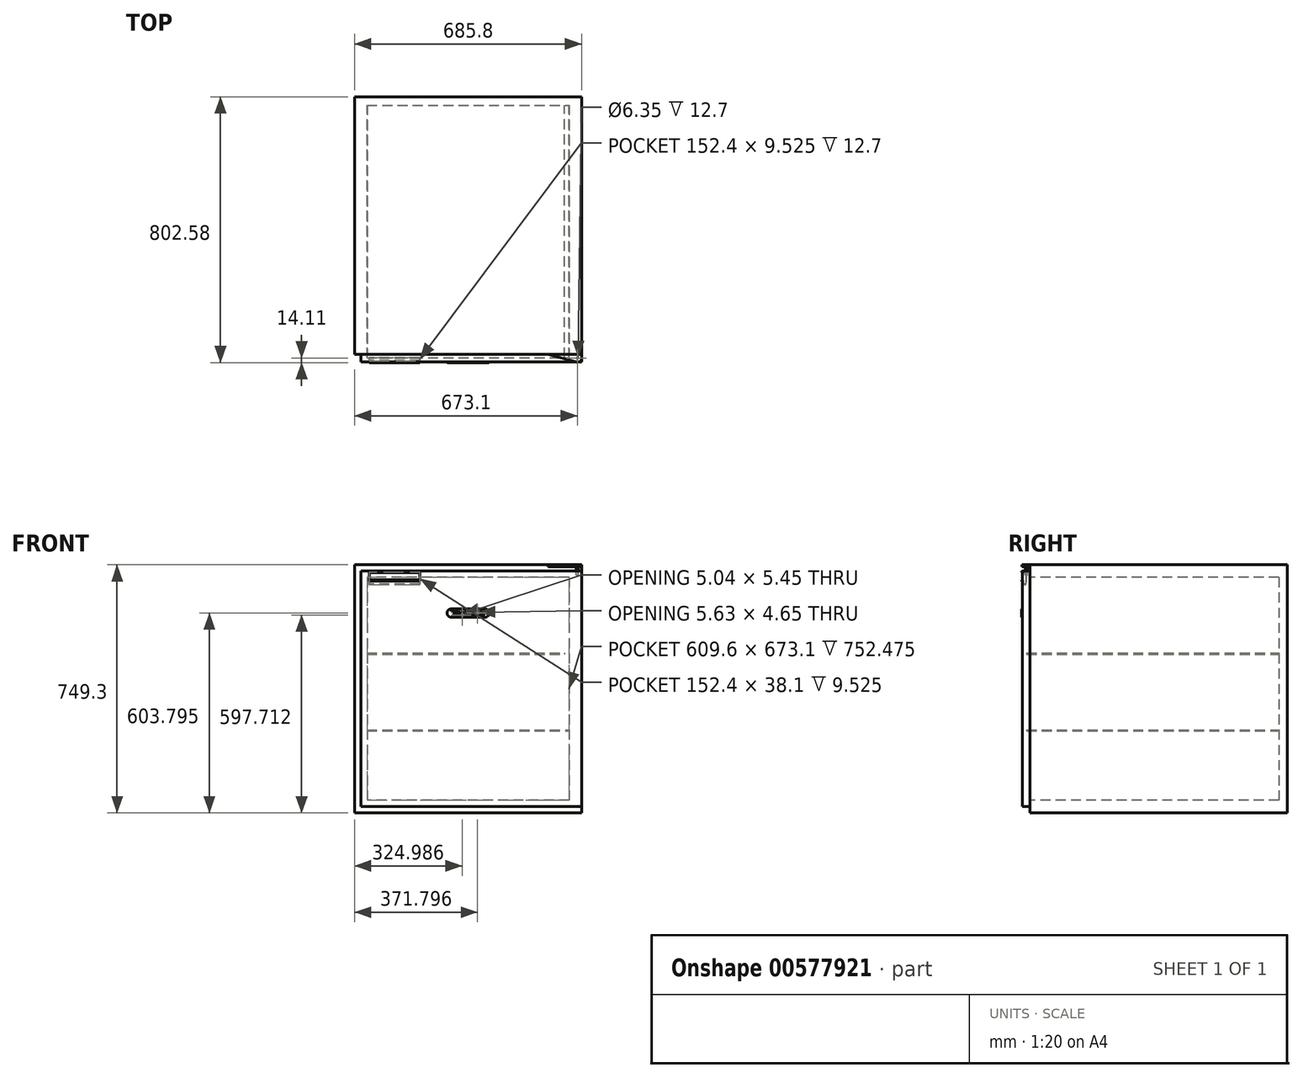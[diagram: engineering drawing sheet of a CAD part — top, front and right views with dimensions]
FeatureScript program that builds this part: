
annotation { "Feature Type Name" : "Feature", "Feature Type Description" : "" }
export const myFeature = defineFeature(function(context is Context, id is Id, definition is map)
    precondition{}
    {
        {
            var Q0;
            Q0=qCreatedBy(makeId("Front.planeOp"),FACE);
            var sketch = newSketch(context, id + "F0", { "sketchPlane" : qUnion([Q0])});
            skLineSegment(sketch, "E0.bottom", {"start": v(342.9, 374.65) * mm, "end": v(-342.9, 374.65) * mm});
            skLineSegment(sketch, "E0.top", {"start": v(342.9, -374.65) * mm, "end": v(-342.9, -374.65) * mm});
            skLineSegment(sketch, "E0.left", {"start": v(342.9, 374.65) * mm, "end": v(342.9, -374.65) * mm});
            skLineSegment(sketch, "E0.right", {"start": v(-342.9, 374.65) * mm, "end": v(-342.9, -374.65) * mm});
            skPoint(sketch, "E0.middle", {"position": v(0, 0) * mm});
            skLineSegment(sketch, "E1.0", {"start": v(304.8, 336.55) * mm, "end": v(-304.8, 336.55) * mm});
            skLineSegment(sketch, "E1.1", {"start": v(304.8, 336.55) * mm, "end": v(304.8, -336.55) * mm});
            skLineSegment(sketch, "E1.2", {"start": v(304.8, -336.55) * mm, "end": v(-304.8, -336.55) * mm});
            skLineSegment(sketch, "E1.3", {"start": v(-304.8, 336.55) * mm, "end": v(-304.8, -336.55) * mm});
            skSolve(sketch);
        }
        {
            var Q0;
            Q0=makeQuery(id+"F0.imprint","IMPRINT",FACE,{"disambiguationData":[TD([[makeQuery(id+"F0.imprint","IMPRINT",EDGE,{"derivedFrom":sQuery(id+"F0.wireOp",EDGE,"E0.bottom")}),1.0]])]});
            extrude(context, id + "F1", {"entities" : qUnion([Q0]), "oppositeDirection" : true, "depth" : 777.88 * mm, "offsetDistance" : 25.4 * mm});
        }
        {
            var Q0;
            Q0=makeQuery(id+"F1.opExtrude","CAP_FACE",FACE,{"disambiguationData":[OSD([sQuery(id+"F0.wireOp",EDGE,"E0.bottom"),sQuery(id+"F0.wireOp",EDGE,"E0.top"),sQuery(id+"F0.wireOp",EDGE,"E0.left"),sQuery(id+"F0.wireOp",EDGE,"E0.right"),sQuery(id+"F0.wireOp",EDGE,"E1.0"),sQuery(id+"F0.wireOp",EDGE,"E1.1"),sQuery(id+"F0.wireOp",EDGE,"E1.2"),sQuery(id+"F0.wireOp",EDGE,"E1.3")])],"isStart":false});
            var sketch = newSketch(context, id + "F2", { "sketchPlane" : qUnion([Q0])});
            skLineSegment(sketch, "E2.0", {"start": v(-342.9, 374.65) * mm, "end": v(342.9, 374.65) * mm});
            skLineSegment(sketch, "E3.0", {"start": v(342.9, 374.65) * mm, "end": v(342.9, -374.65) * mm});
            skLineSegment(sketch, "E3.1", {"start": v(-342.9, 374.65) * mm, "end": v(-342.9, -374.65) * mm});
            skLineSegment(sketch, "E3.2", {"start": v(-342.9, -374.65) * mm, "end": v(342.9, -374.65) * mm});
            skSolve(sketch);
        }
        {
            var Q0;
            Q0 = qSketchRegion(id + "F2", true);
            extrude(context, id + "F3", {"entities" : qUnion([Q0]), "operationType" : NewBodyOperationType.ADD, "oppositeDirection" : true, "depth" : 25.4 * mm, "offsetDistance" : 25.4 * mm});
        }
        {
            var Q0;
            Q0=makeQuery(id+"F3.opExtrude","CAP_FACE",FACE,{"disambiguationData":[OSD([sQuery(id+"F2.wireOp",EDGE,"E2.0"),sQuery(id+"F2.wireOp",EDGE,"E3.0"),sQuery(id+"F2.wireOp",EDGE,"E3.1"),sQuery(id+"F2.wireOp",EDGE,"E3.2")])],"isStart":false});
            var sketch = newSketch(context, id + "F4", { "sketchPlane" : qUnion([Q0])});
            skLineSegment(sketch, "E4.bottom", {"start": v(-304.8, 107.95) * mm, "end": v(290.97, 107.95) * mm});
            skLineSegment(sketch, "E4.top", {"start": v(-304.8, 104.78) * mm, "end": v(290.97, 104.78) * mm});
            skLineSegment(sketch, "E4.left", {"start": v(-304.8, 107.95) * mm, "end": v(-304.8, 104.78) * mm});
            skLineSegment(sketch, "E4.right", {"start": v(290.97, 107.95) * mm, "end": v(290.97, 104.78) * mm});
            skLineSegment(sketch, "E5.bottom", {"start": v(-304.8, -123.82) * mm, "end": v(304.8, -123.82) * mm});
            skLineSegment(sketch, "E5.top", {"start": v(-304.8, -127) * mm, "end": v(304.8, -127) * mm});
            skLineSegment(sketch, "E5.left", {"start": v(-304.8, -123.82) * mm, "end": v(-304.8, -127) * mm});
            skLineSegment(sketch, "E5.right", {"start": v(304.8, -123.82) * mm, "end": v(304.8, -127) * mm});
            skSolve(sketch);
        }
        {
            var Q0;
            Q0 = qSketchRegion(id + "F4", true);
            extrude(context, id + "F5", {"entities" : qUnion([Q0]), "depth" : 762 * mm, "offsetDistance" : 25.4 * mm});
        }
        {
            var Q0;
            Q0=makeQuery(id+"F1.opExtrude","CAP_FACE",FACE,{"disambiguationData":[OSD([sQuery(id+"F0.wireOp",EDGE,"E0.bottom"),sQuery(id+"F0.wireOp",EDGE,"E0.top"),sQuery(id+"F0.wireOp",EDGE,"E0.left"),sQuery(id+"F0.wireOp",EDGE,"E0.right"),sQuery(id+"F0.wireOp",EDGE,"E1.0"),sQuery(id+"F0.wireOp",EDGE,"E1.1"),sQuery(id+"F0.wireOp",EDGE,"E1.2"),sQuery(id+"F0.wireOp",EDGE,"E1.3")])],"isStart":true});
            var sketch = newSketch(context, id + "F6", { "sketchPlane" : qUnion([Q0])});
            skLineSegment(sketch, "E6.0", {"start": v(342.9, 355.6) * mm, "end": v(-323.85, 355.6) * mm});
            skLineSegment(sketch, "E6.2", {"start": v(342.9, -355.6) * mm, "end": v(-323.85, -355.6) * mm});
            skLineSegment(sketch, "E6.3", {"start": v(-323.85, 355.6) * mm, "end": v(-323.85, -355.6) * mm});
            skLineSegment(sketch, "E7", {"start": v(342.9, 355.6) * mm, "end": v(342.9, -355.6) * mm});
            skSolve(sketch);
        }
        {
            var Q0;
            Q0 = qSketchRegion(id + "F6", true);
            extrude(context, id + "F7", {"entities" : qUnion([Q0]), "depth" : 22.86 * mm, "offsetDistance" : 25.4 * mm});
        }
        {
            var Q0;
            Q0=makeQuery(id+"F1.opExtrude","SWEPT_FACE",FACE,{"disambiguationData":[OSD([sQuery(id+"F0.wireOp",EDGE,"E0.bottom")])]});
            var sketch = newSketch(context, id + "F8", { "sketchPlane" : qUnion([Q0])});
            skLineSegment(sketch, "E8", {"start": v(241.3, 0) * mm, "end": v(326.92, -22.86) * mm});
            skLineSegment(sketch, "E9", {"start": v(342.9, -10.59) * mm, "end": v(342.9, 0) * mm});
            skPoint(sketch, "E10.0", {"position": v(-323.85, -22.86) * mm});
            skLineSegment(sketch, "E11", {"start": v(241.3, 0) * mm, "end": v(342.9, 0) * mm});
            skPoint(sketch, "E12.visualSharp", {"position": v(342.9, -27.13) * mm});
            skArc(sketch, "E12.filletArc", {"start": v(326.92, -22.86) * mm, "mid": v(337.94, -20.66) * mm, "end": v(342.9, -10.59) * mm});
            skSolve(sketch);
        }
        {
            var Q0;
            Q0 = qSketchRegion(id + "F8", true);
            extrude(context, id + "F9", {"entities" : qUnion([Q0]), "oppositeDirection" : true, "depth" : 6.35 * mm, "offsetDistance" : 25.4 * mm});
        }
        {
            var Q0;
            Q0=makeQuery(id+"F9.opExtrude","CAP_FACE",FACE,{"disambiguationData":[OSD([sQuery(id+"F8.wireOp",EDGE,"E8"),sQuery(id+"F8.wireOp",EDGE,"E9"),sQuery(id+"F8.wireOp",EDGE,"E11"),sQuery(id+"F8.wireOp",EDGE,"E12.filletArc")])],"isStart":false});
            var sketch = newSketch(context, id + "F10", { "sketchPlane" : qUnion([Q0])});
            skCircle(sketch, "E13", {"center": v(330.2, 10.59) * mm, "radius": 3.18 * mm});
            skSolve(sketch);
        }
        {
            var Q0;
            Q0 = qSketchRegion(id + "F10", true);
            extrude(context, id + "F11", {"entities" : qUnion([Q0]), "operationType" : NewBodyOperationType.ADD, "depth" : 25.4 * mm, "offsetDistance" : 25.4 * mm});
        }
        {
            var Q0;
            Q0=makeQuery(id+"F7.opExtrude","SWEPT_FACE",FACE,{"disambiguationData":[OSD([sQuery(id+"F6.wireOp",EDGE,"E6.0")])]});
            var sketch = newSketch(context, id + "F12", { "sketchPlane" : qUnion([Q0])});
            skCircle(sketch, "E14", {"center": v(330.2, -10.59) * mm, "radius": 3.17 * mm});
            skSolve(sketch);
        }
        {
            var Q0;
            Q0 = qSketchRegion(id + "F12", true);
            extrude(context, id + "F13", {"entities" : qUnion([Q0]), "operationType" : NewBodyOperationType.REMOVE, "oppositeDirection" : true, "depth" : 12.7 * mm, "offsetDistance" : 25.4 * mm});
        }
        {
            var Q0;
            Q0=makeQuery(id+"F7.opExtrude","SWEPT_FACE",FACE,{"disambiguationData":[OSD([sQuery(id+"F6.wireOp",EDGE,"E6.3")])]});
            cPlane(context, id + "F14", {"entities" : qUnion([Q0]), "cplaneType" : CPlaneType.OFFSET, "offset" : 25.4 * mm, "oppositeDirection" : true, "width" : 152.4 * mm, "height" : 152.4 * mm});
        }
        {
            var Q0;
            Q0=qCreatedBy(id+"F14.planeOp",FACE);
            var sketch = newSketch(context, id + "F15", { "sketchPlane" : qUnion([Q0])});
            skPoint(sketch, "E15.0", {"position": v(22.86, 355.6) * mm});
            skLineSegment(sketch, "E16", {"start": v(22.86, 352.43) * mm, "end": v(10.16, 352.43) * mm});
            skLineSegment(sketch, "E17", {"start": v(10.16, 352.43) * mm, "end": v(10.16, 314.33) * mm});
            skLineSegment(sketch, "E18", {"start": v(10.16, 314.33) * mm, "end": v(19.69, 314.33) * mm});
            skLineSegment(sketch, "E19", {"start": v(19.69, 314.33) * mm, "end": v(19.69, 327.03) * mm});
            skLineSegment(sketch, "E20", {"start": v(19.69, 327.03) * mm, "end": v(22.86, 327.03) * mm});
            skLineSegment(sketch, "E21", {"start": v(22.86, 352.43) * mm, "end": v(22.86, 327.03) * mm});
            skSolve(sketch);
        }
        {
            var Q0;
            Q0 = qSketchRegion(id + "F15", true);
            extrude(context, id + "F16", {"entities" : qUnion([Q0]), "operationType" : NewBodyOperationType.REMOVE, "oppositeDirection" : true, "depth" : 152.4 * mm, "offsetDistance" : 25.4 * mm});
        }
        {
            var Q0;
            Q0=qCreatedBy(id+"F14.planeOp",FACE);
            var sketch = newSketch(context, id + "F17", { "sketchPlane" : qUnion([Q0])});
            skPoint(sketch, "E22.0", {"position": v(22.86, 355.6) * mm});
            skLineSegment(sketch, "E23", {"start": v(22.86, 352.43) * mm, "end": v(10.16, 352.43) * mm});
            skLineSegment(sketch, "E24", {"start": v(10.16, 352.43) * mm, "end": v(10.16, 314.33) * mm});
            skLineSegment(sketch, "E25", {"start": v(10.16, 314.33) * mm, "end": v(19.69, 314.33) * mm});
            skLineSegment(sketch, "E26", {"start": v(19.69, 314.33) * mm, "end": v(19.69, 327.03) * mm});
            skLineSegment(sketch, "E27", {"start": v(19.69, 327.03) * mm, "end": v(22.86, 327.03) * mm});
            skLineSegment(sketch, "E28.1", {"start": v(11.75, 350.84) * mm, "end": v(11.75, 315.91) * mm});
            skLineSegment(sketch, "E28.2", {"start": v(22.86, 350.84) * mm, "end": v(11.75, 350.84) * mm});
            skLineSegment(sketch, "E29.0", {"start": v(11.75, 315.91) * mm, "end": v(18.1, 315.91) * mm});
            skLineSegment(sketch, "E30", {"start": v(18.1, 315.91) * mm, "end": v(18.1, 328.61) * mm});
            skLineSegment(sketch, "E31", {"start": v(18.1, 328.61) * mm, "end": v(24.45, 328.61) * mm});
            skLineSegment(sketch, "E32", {"start": v(22.86, 350.84) * mm, "end": v(24.45, 350.84) * mm});
            skLineSegment(sketch, "E33", {"start": v(24.45, 350.84) * mm, "end": v(24.45, 354.01) * mm});
            skLineSegment(sketch, "E34", {"start": v(24.45, 354.01) * mm, "end": v(22.86, 354.01) * mm});
            skLineSegment(sketch, "E35", {"start": v(22.86, 354.01) * mm, "end": v(22.86, 352.43) * mm});
            skLineSegment(sketch, "E36", {"start": v(24.45, 328.61) * mm, "end": v(24.45, 325.44) * mm});
            skLineSegment(sketch, "E37", {"start": v(24.45, 325.44) * mm, "end": v(22.86, 325.44) * mm});
            skLineSegment(sketch, "E38", {"start": v(22.86, 325.44) * mm, "end": v(22.86, 327.03) * mm});
            skSolve(sketch);
        }
        {
            var Q0;
            Q0 = qSketchRegion(id + "F17", true);
            extrude(context, id + "F18", {"entities" : qUnion([Q0]), "oppositeDirection" : true, "depth" : 152.4 * mm, "offsetDistance" : 25.4 * mm});
        }
        {
            var Q0;
            Q0=makeQuery(id+"F18.opExtrude","SWEPT_EDGE",EDGE,{"disambiguationData":[OSD([sQuery(id+"F17.wireOp",EDGE,"E32"),sQuery(id+"F17.wireOp",EDGE,"E33")])]});
            var Q1;
            Q1=makeQuery(id+"F18.opExtrude","SWEPT_EDGE",EDGE,{"disambiguationData":[OSD([sQuery(id+"F17.wireOp",EDGE,"E31"),sQuery(id+"F17.wireOp",EDGE,"E36")])]});
            var Q2;
            Q2=makeQuery(id+"F18.opExtrude","SWEPT_EDGE",EDGE,{"disambiguationData":[OSD([sQuery(id+"F17.wireOp",EDGE,"E30"),sQuery(id+"F17.wireOp",EDGE,"E31")])]});
            var Q3;
            Q3=makeQuery(id+"F18.opExtrude","SWEPT_EDGE",EDGE,{"disambiguationData":[OSD([sQuery(id+"F17.wireOp",EDGE,"E28.1"),sQuery(id+"F17.wireOp",EDGE,"E28.2")])]});
            fillet(context, id + "F19", {"entities" : qUnion([Q0, Q1, Q2, Q3]), "radius" : 3.17 * mm, "tangentPropagation" : true, "allowEdgeOverflow" : false});
        }
        {
            var Q0;
            Q0=makeQuery(id+"F7.opExtrude","CAP_FACE",FACE,{"disambiguationData":[OSD([sQuery(id+"F6.wireOp",EDGE,"E6.0"),sQuery(id+"F6.wireOp",EDGE,"E6.2"),sQuery(id+"F6.wireOp",EDGE,"E6.3"),sQuery(id+"F6.wireOp",EDGE,"E7")])],"isStart":false});
            var sketch = newSketch(context, id + "F20", { "sketchPlane" : qUnion([Q0])});
            skLineSegment(sketch, "E39", {"start": v(-50.8, 228.6) * mm, "end": v(50.8, 228.6) * mm});
            skPoint(sketch, "E40", {"position": v(0, 228.6) * mm});
            skArc(sketch, "E41.0.startCap", {"start": v(-50.8, 215.9) * mm, "mid": v(-63.5, 228.6) * mm, "end": v(-50.8, 241.3) * mm});
            skArc(sketch, "E41.0.endCap", {"start": v(50.8, 241.3) * mm, "mid": v(63.5, 228.6) * mm, "end": v(50.8, 215.9) * mm});
            skLineSegment(sketch, "E41.0.left", {"start": v(-50.8, 241.3) * mm, "end": v(50.8, 241.3) * mm});
            skLineSegment(sketch, "E41.0.right", {"start": v(-50.8, 215.9) * mm, "end": v(50.8, 215.9) * mm});
            skSolve(sketch);
        }
        {
            var Q0;
            Q0 = qSketchRegion(id + "F20", true);
            extrude(context, id + "F21", {"entities" : qUnion([Q0]), "depth" : 1.59 * mm, "offsetDistance" : 25.4 * mm});
        }
        {
            var Q0;
            Q0=makeQuery(id+"F21.opExtrude","CAP_FACE",FACE,{"disambiguationData":[OSD([sQuery(id+"F20.wireOp",EDGE,"E41.0.startCap"),sQuery(id+"F20.wireOp",EDGE,"E41.0.endCap"),sQuery(id+"F20.wireOp",EDGE,"E41.0.left"),sQuery(id+"F20.wireOp",EDGE,"E41.0.right")])],"isStart":false});
            fillet(context, id + "F22", {"entities" : qUnion([Q0]), "radius" : 1.59 * mm, "tangentPropagation" : true, "allowEdgeOverflow" : false});
        }
        {
            var Q0;
            Q0=makeQuery(id+"F21.opExtrude","CAP_FACE",FACE,{"disambiguationData":[OSD([sQuery(id+"F20.wireOp",EDGE,"E41.0.startCap"),sQuery(id+"F20.wireOp",EDGE,"E41.0.endCap"),sQuery(id+"F20.wireOp",EDGE,"E41.0.left"),sQuery(id+"F20.wireOp",EDGE,"E41.0.right")])],"isStart":false});
            var sketch = newSketch(context, id + "F23", { "sketchPlane" : qUnion([Q0])});
            skText(sketch, "E42", { "text": "Traulsen", "fontName": "Tinos-Regular.ttf"});
            const initialGuessF23  = {"E42": [-0.05082, 0.21908, 1, 0, 0.02064]};
            skSetInitialGuess(sketch, initialGuessF23);
            skSolve(sketch);
        }
        {
            var Q0;
            Q0 = qSketchRegion(id + "F23", true);
            extrude(context, id + "F24", {"entities" : qUnion([Q0]), "depth" : 0.25 * mm, "offsetDistance" : 25.4 * mm});
        }
    });
